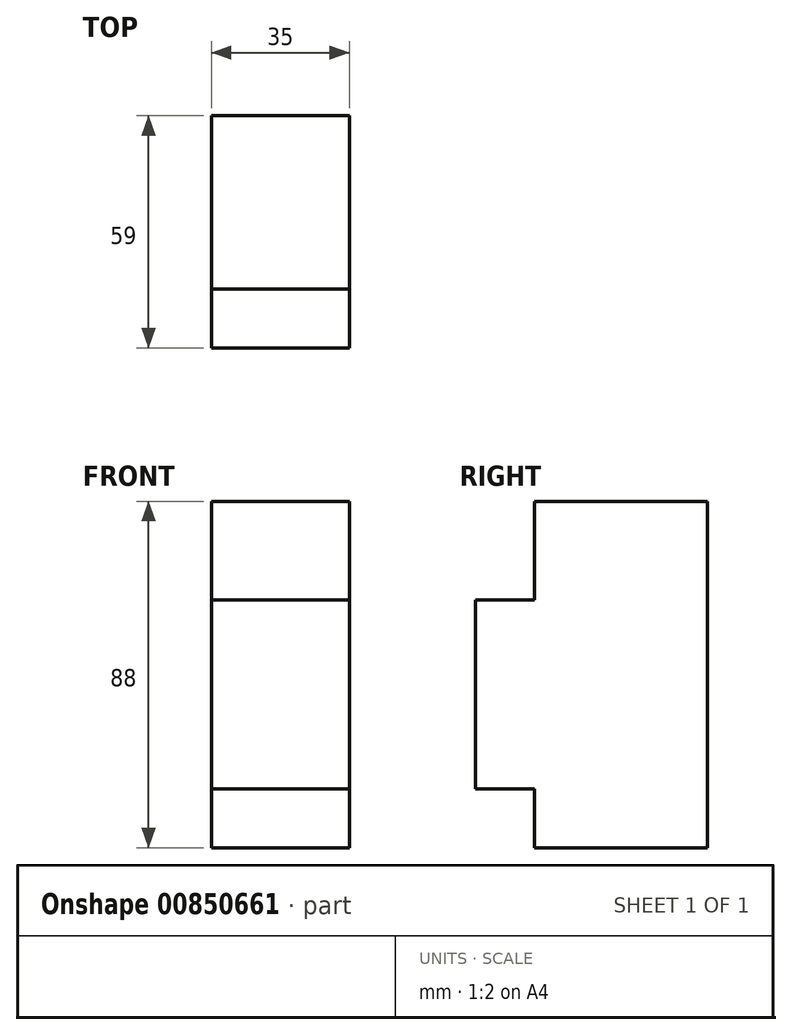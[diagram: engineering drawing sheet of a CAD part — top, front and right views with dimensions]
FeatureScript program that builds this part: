
annotation { "Feature Type Name" : "Feature", "Feature Type Description" : "" }
export const myFeature = defineFeature(function(context is Context, id is Id, definition is map)
    precondition{}
    {
        {
            var Q0;
            Q0=qCreatedBy(makeId("Right.planeOp"),FACE);
            var sketch = newSketch(context, id + "F0", { "sketchPlane" : qUnion([Q0])});
            skLineSegment(sketch, "E0", {"start": v(-52.15, 31.57) * mm, "end": v(-52.15, -16.43) * mm});
            skLineSegment(sketch, "E1", {"start": v(-52.15, -16.43) * mm, "end": v(-37.15, -16.43) * mm});
            skLineSegment(sketch, "E2", {"start": v(-37.15, -16.43) * mm, "end": v(-37.15, -31.43) * mm});
            skLineSegment(sketch, "E3", {"start": v(-37.15, -31.43) * mm, "end": v(6.85, -31.43) * mm});
            skLineSegment(sketch, "E4", {"start": v(6.85, -31.43) * mm, "end": v(6.85, 56.57) * mm});
            skLineSegment(sketch, "E5", {"start": v(6.85, 56.57) * mm, "end": v(-37.15, 56.57) * mm});
            skLineSegment(sketch, "E6", {"start": v(-37.15, 56.57) * mm, "end": v(-37.15, 31.57) * mm});
            skLineSegment(sketch, "E7", {"start": v(-37.15, 31.57) * mm, "end": v(-52.15, 31.57) * mm});
            skSolve(sketch);
        }
        {
            var Q0;
            Q0 = qSketchRegion(id + "F0", true);
            extrude(context, id + "F1", {"entities" : qUnion([Q0]), "depth" : 35 * mm, "offsetDistance" : 25 * mm});
        }
    });
